# Revit family: Seat-LaZBoy-KM1900F
name_source: partatom
category: Furniture
revit_build: Autodesk Revit 2017 (Build: 20160225_1515(x64)
units: mm (PartAtom-declared; Revit-internal decimal feet)

## family parameters
Always vertical = Yes
Cut with Voids When Loaded = No
OmniClass Number = 23.40.20.00
OmniClass Title = General Furniture and Specialties
Room Calculation Point = No
Shared = No
Work Plane-Based = No

## types (4) — shared parameters
Armcap Material = <By Category>
Assembly Code = E2020200
Depth = 34.25"
Height = 34.50"
Manufacturer = LaZBoy
Product Documentation Link = URL
URL = https://www.la-z-boy.com
Width = 53.00"

## per-type parameters (varying)
| type | Description | Model | With Armcap |
| 53", Upholstered Arms | 53" Chair with casters and upholstered arm caps | KM1900F | No |
| 53", Urethane Arm Caps | 53" Chair with casters and urethane arm caps | KM1900U | Yes |
| 53", Wood Arm Caps | 53" Chair with casters and wood arm caps | KM1900W | Yes |
| 53", Solid Surface Arm Caps | 53" Chair with casters and solid surface arm caps | KM1900J | Yes |

## geometry (parser evidence)
native form markers: Sweep x8
no freeform markers — native parametric forms only
